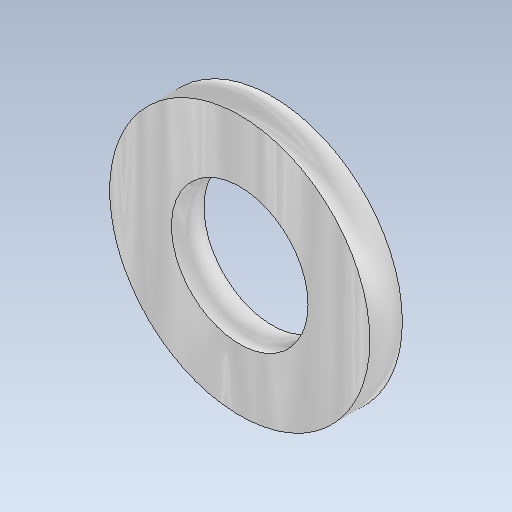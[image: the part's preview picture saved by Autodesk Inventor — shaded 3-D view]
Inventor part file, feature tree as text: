
AUTODESK INVENTOR PART (.ipt)
format: ipt  version: 2020.2 (Build 242310000, 310)  size: 124,928 bytes
history: native  units: mm
features: other x1, extrude x1, sketch x1
ambient origin geometry x8: Origin, YZ Plane, XZ Plane, XY Plane, X Axis, Y Axis, Z Axis, Center Point
bodies: Body1 (feature_tree)
feature tree (3):
  other  "ソリッド1"
  extrude  "押し出し1"  Depth=8.0mm
  sketch  "スケッチ1"
